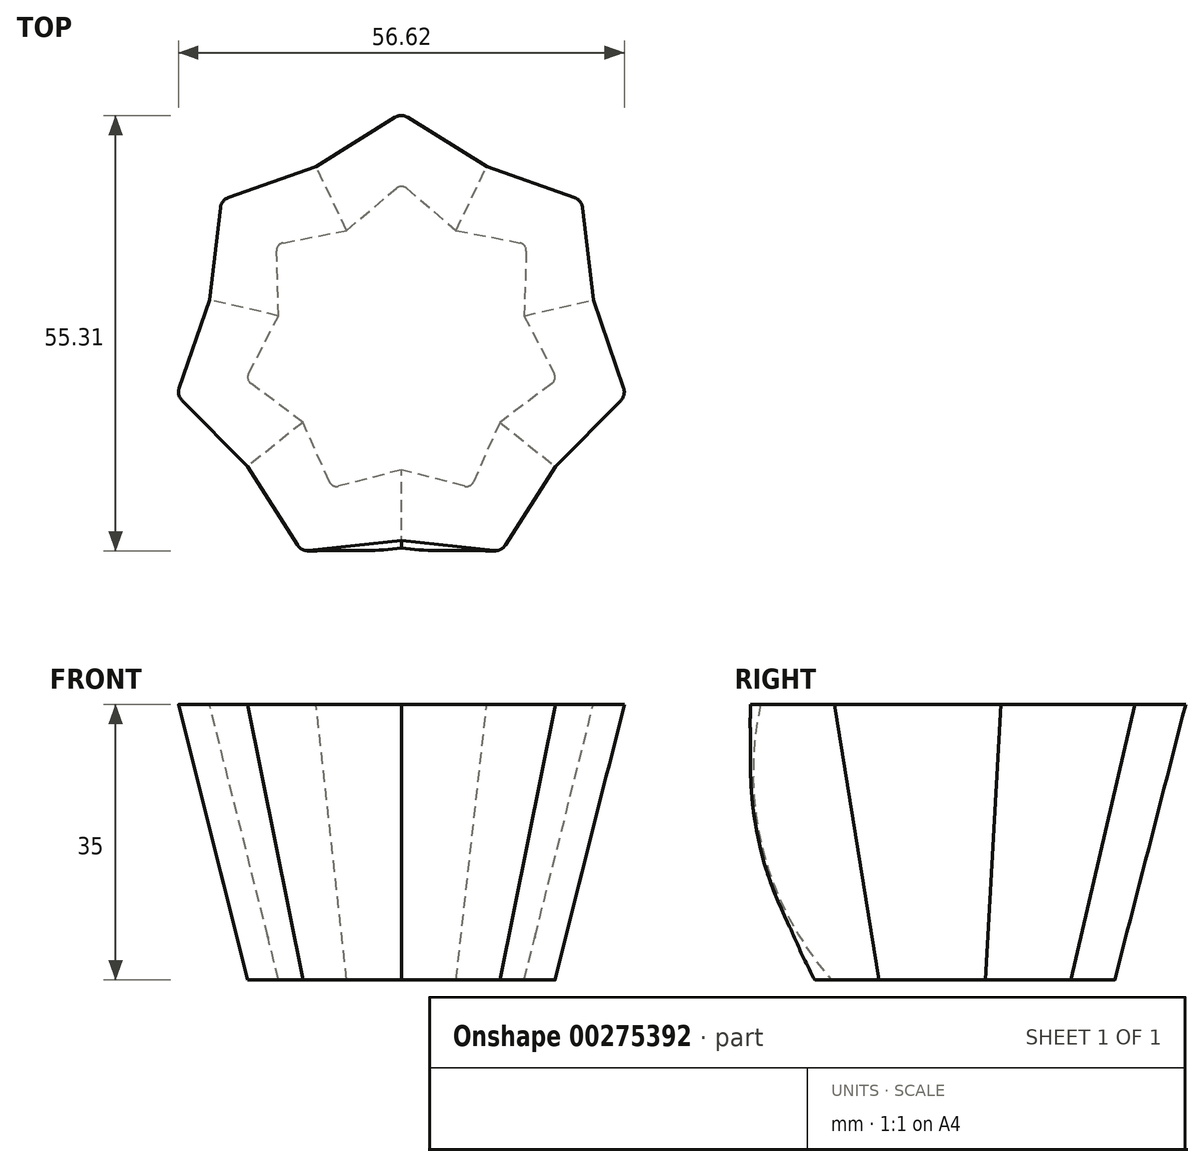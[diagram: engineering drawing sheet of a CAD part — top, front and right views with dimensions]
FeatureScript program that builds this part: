
annotation { "Feature Type Name" : "Feature", "Feature Type Description" : "" }
export const myFeature = defineFeature(function(context is Context, id is Id, definition is map)
    precondition{}
    {
        {
            var Q0;
            Q0=qCreatedBy(makeId("Top.planeOp"),FACE);
            var sketch = newSketch(context, id + "F0", { "sketchPlane" : qUnion([Q0])});
            skCircle(sketch, "E0", {"center": v(0, 0) * mm, "radius": 20 * mm, "construction": true});
            skCircle(sketch, "E1", {"center": v(0, 0) * mm, "radius": 16 * mm, "construction": true});
            skLineSegment(sketch, "E2", {"start": v(-6.94, 14.42) * mm, "end": v(-0.65, 19.76) * mm});
            skLineSegment(sketch, "E3", {"start": v(0.65, 19.76) * mm, "end": v(6.94, 14.42) * mm});
            skPoint(sketch, "E4.visualSharp", {"position": v(0, 20.31) * mm});
            skArc(sketch, "E4.filletArc", {"start": v(0.65, 19.76) * mm, "mid": v(0, 20) * mm, "end": v(-0.65, 19.76) * mm});
            skPoint(sketch, "E5.1.0", {"position": v(-15.88, 12.66) * mm});
            skLineSegment(sketch, "E5.1.1", {"start": v(-15.05, 12.83) * mm, "end": v(-6.94, 14.42) * mm});
            skLineSegment(sketch, "E5.1.2", {"start": v(-15.6, 3.56) * mm, "end": v(-15.85, 11.82) * mm});
            skArc(sketch, "E5.1.3", {"start": v(-15.05, 12.83) * mm, "mid": v(-15.64, 12.47) * mm, "end": v(-15.85, 11.82) * mm});
            skPoint(sketch, "E5.2.0", {"position": v(-19.8, -4.52) * mm});
            skLineSegment(sketch, "E5.2.1", {"start": v(-19.41, -3.77) * mm, "end": v(-15.6, 3.56) * mm});
            skLineSegment(sketch, "E5.2.2", {"start": v(-12.5, -9.98) * mm, "end": v(-19.12, -5.03) * mm});
            skArc(sketch, "E5.2.3", {"start": v(-19.41, -3.77) * mm, "mid": v(-19.5, -4.45) * mm, "end": v(-19.12, -5.03) * mm});
            skPoint(sketch, "E5.3.0", {"position": v(-8.81, -18.3) * mm});
            skLineSegment(sketch, "E5.3.1", {"start": v(-9.16, -17.52) * mm, "end": v(-12.5, -9.98) * mm});
            skLineSegment(sketch, "E5.3.2", {"start": v(0, -16) * mm, "end": v(-8, -18.09) * mm});
            skArc(sketch, "E5.3.3", {"start": v(-9.16, -17.52) * mm, "mid": v(-8.68, -18.02) * mm, "end": v(-8, -18.09) * mm});
            skPoint(sketch, "E5.4.0", {"position": v(8.81, -18.3) * mm});
            skLineSegment(sketch, "E5.4.1", {"start": v(8, -18.09) * mm, "end": v(0, -16) * mm});
            skLineSegment(sketch, "E5.4.2", {"start": v(12.5, -9.98) * mm, "end": v(9.16, -17.52) * mm});
            skArc(sketch, "E5.4.3", {"start": v(8, -18.09) * mm, "mid": v(8.68, -18.02) * mm, "end": v(9.16, -17.52) * mm});
            skPoint(sketch, "E5.5.0", {"position": v(19.8, -4.52) * mm});
            skLineSegment(sketch, "E5.5.1", {"start": v(19.12, -5.03) * mm, "end": v(12.5, -9.98) * mm});
            skLineSegment(sketch, "E5.5.2", {"start": v(15.6, 3.56) * mm, "end": v(19.41, -3.77) * mm});
            skArc(sketch, "E5.5.3", {"start": v(19.12, -5.03) * mm, "mid": v(19.5, -4.45) * mm, "end": v(19.41, -3.77) * mm});
            skPoint(sketch, "E5.6.0", {"position": v(15.88, 12.66) * mm});
            skLineSegment(sketch, "E5.6.1", {"start": v(15.85, 11.82) * mm, "end": v(15.6, 3.56) * mm});
            skLineSegment(sketch, "E5.6.2", {"start": v(6.94, 14.42) * mm, "end": v(15.05, 12.83) * mm});
            skArc(sketch, "E5.6.3", {"start": v(15.85, 11.82) * mm, "mid": v(15.64, 12.47) * mm, "end": v(15.05, 12.83) * mm});
            skSolve(sketch);
        }
        {
            var Q0;
            Q0=qCreatedBy(makeId("Top.planeOp"),FACE);
            cPlane(context, id + "F1", {"entities" : qUnion([Q0]), "cplaneType" : CPlaneType.OFFSET, "offset" : 35 * mm, "width" : 150 * mm, "height" : 150 * mm});
        }
        {
            var Q0;
            Q0=qCreatedBy(id+"F1.planeOp",FACE);
            var sketch = newSketch(context, id + "F2", { "sketchPlane" : qUnion([Q0])});
            skCircle(sketch, "E6", {"center": v(0, 0) * mm, "radius": 29 * mm, "construction": true});
            skCircle(sketch, "E7", {"center": v(0, 0) * mm, "radius": 25 * mm, "construction": true});
            skLineSegment(sketch, "E8", {"start": v(-10.85, 22.52) * mm, "end": v(-0.8, 28.77) * mm});
            skLineSegment(sketch, "E9", {"start": v(10.85, 22.52) * mm, "end": v(0.8, 28.77) * mm});
            skPoint(sketch, "E10.visualSharp", {"position": v(0, 29.27) * mm});
            skArc(sketch, "E10.filletArc", {"start": v(0.8, 28.77) * mm, "mid": v(0, 29) * mm, "end": v(-0.8, 28.77) * mm});
            skLineSegment(sketch, "E11.1.0", {"start": v(-10.85, 22.52) * mm, "end": v(-22, 18.56) * mm});
            skArc(sketch, "E11.1.1", {"start": v(-22, 18.56) * mm, "mid": v(-22.67, 18.08) * mm, "end": v(-23, 17.32) * mm});
            skLineSegment(sketch, "E11.1.2", {"start": v(-24.37, 5.56) * mm, "end": v(-23, 17.32) * mm});
            skPoint(sketch, "E11.1.3", {"position": v(-22.88, 18.25) * mm});
            skLineSegment(sketch, "E11.2.0", {"start": v(-24.37, 5.56) * mm, "end": v(-28.23, -5.63) * mm});
            skArc(sketch, "E11.2.1", {"start": v(-28.23, -5.63) * mm, "mid": v(-28.27, -6.45) * mm, "end": v(-27.88, -7.17) * mm});
            skLineSegment(sketch, "E11.2.2", {"start": v(-19.55, -15.59) * mm, "end": v(-27.88, -7.17) * mm});
            skPoint(sketch, "E11.2.3", {"position": v(-28.53, -6.51) * mm});
            skLineSegment(sketch, "E11.3.0", {"start": v(-19.55, -15.59) * mm, "end": v(-13.2, -25.58) * mm});
            skArc(sketch, "E11.3.1", {"start": v(-13.2, -25.58) * mm, "mid": v(-12.58, -26.13) * mm, "end": v(-11.77, -26.27) * mm});
            skLineSegment(sketch, "E11.3.2", {"start": v(0, -25) * mm, "end": v(-11.77, -26.27) * mm});
            skPoint(sketch, "E11.3.3", {"position": v(-12.7, -26.37) * mm});
            skLineSegment(sketch, "E11.4.0", {"start": v(0, -25) * mm, "end": v(11.77, -26.27) * mm});
            skArc(sketch, "E11.4.1", {"start": v(11.77, -26.27) * mm, "mid": v(12.58, -26.13) * mm, "end": v(13.2, -25.58) * mm});
            skLineSegment(sketch, "E11.4.2", {"start": v(19.55, -15.59) * mm, "end": v(13.2, -25.58) * mm});
            skPoint(sketch, "E11.4.3", {"position": v(12.7, -26.37) * mm});
            skLineSegment(sketch, "E11.5.0", {"start": v(19.55, -15.59) * mm, "end": v(27.88, -7.17) * mm});
            skArc(sketch, "E11.5.1", {"start": v(27.88, -7.17) * mm, "mid": v(28.27, -6.45) * mm, "end": v(28.23, -5.63) * mm});
            skLineSegment(sketch, "E11.5.2", {"start": v(24.37, 5.56) * mm, "end": v(28.23, -5.63) * mm});
            skPoint(sketch, "E11.5.3", {"position": v(28.53, -6.51) * mm});
            skLineSegment(sketch, "E11.6.0", {"start": v(24.37, 5.56) * mm, "end": v(23, 17.32) * mm});
            skArc(sketch, "E11.6.1", {"start": v(23, 17.32) * mm, "mid": v(22.67, 18.08) * mm, "end": v(22, 18.56) * mm});
            skLineSegment(sketch, "E11.6.2", {"start": v(10.85, 22.52) * mm, "end": v(22, 18.56) * mm});
            skPoint(sketch, "E11.6.3", {"position": v(22.88, 18.25) * mm});
            skSolve(sketch);
        }
        {
            var Q0;
            Q0=qCreatedBy(makeId("Right.planeOp"),FACE);
            var sketch = newSketch(context, id + "F3", { "sketchPlane" : qUnion([Q0])});
            skArc(sketch, "E12", {"start": v(-25, 35) * mm, "mid": v(-24.68, 16.43) * mm, "end": v(-16, 0) * mm});
            skSolve(sketch);
        }
        {
            var Q0;
            Q0=makeQuery(id+"F0.imprint","IMPRINT",FACE,{"disambiguationData":[TD([[makeQuery(id+"F0.imprint","IMPRINT",EDGE,{"derivedFrom":sQuery(id+"F0.wireOp",EDGE,"E2")}),-1.0]])]});
            var Q1;
            Q1=makeQuery(id+"F2.imprint","IMPRINT",FACE,{"disambiguationData":[TD([[makeQuery(id+"F2.imprint","IMPRINT",EDGE,{"derivedFrom":sQuery(id+"F2.wireOp",EDGE,"E8")}),-1.0]])]});
            var Q2;
            Q2=sQuery(id+"F02dZpxoTDiz8ow_0.6.F3.wireOp",EDGE,"E12");
            var Q3;
            Q3=sQuery(id+"F3.wireOp",EDGE,"E12");
            var Q4;
            Q4=sQuery(id+"F02dZpxoTDiz8ow_0.1.F3.wireOp",EDGE,"E12");
            var Q5;
            Q5=sQuery(id+"F02dZpxoTDiz8ow_0.2.F3.wireOp",EDGE,"E12");
            var Q6;
            Q6=sQuery(id+"F02dZpxoTDiz8ow_0.3.F3.wireOp",EDGE,"E12");
            var Q7;
            Q7=sQuery(id+"F02dZpxoTDiz8ow_0.4.F3.wireOp",EDGE,"E12");
            var Q8;
            Q8=sQuery(id+"F02dZpxoTDiz8ow_0.5.F3.wireOp",EDGE,"E12");
            loft(context, id + "F4", {"addGuides" : true, "sheetProfilesArray" : [{ "sheetProfileEntities" : qUnion([Q0]) }, { "sheetProfileEntities" : qUnion([Q1]) }], "guidesArray" : [{ "guideEntities" : qUnion([Q2]), "guideDerivativeType" : LoftGuideDerivativeType.DEFAULT, "guideDerivativeMagnitude" : 1 }, { "guideEntities" : qUnion([Q3]), "guideDerivativeType" : LoftGuideDerivativeType.DEFAULT, "guideDerivativeMagnitude" : 1 }, { "guideEntities" : qUnion([Q4]), "guideDerivativeType" : LoftGuideDerivativeType.DEFAULT, "guideDerivativeMagnitude" : 1 }, { "guideEntities" : qUnion([Q5]), "guideDerivativeType" : LoftGuideDerivativeType.DEFAULT, "guideDerivativeMagnitude" : 1 }, { "guideEntities" : qUnion([Q6]), "guideDerivativeType" : LoftGuideDerivativeType.DEFAULT, "guideDerivativeMagnitude" : 1 }, { "guideEntities" : qUnion([Q7]), "guideDerivativeType" : LoftGuideDerivativeType.DEFAULT, "guideDerivativeMagnitude" : 1 }, { "guideEntities" : qUnion([Q8]), "guideDerivativeType" : LoftGuideDerivativeType.DEFAULT, "guideDerivativeMagnitude" : 1 }]});
        }
    });
